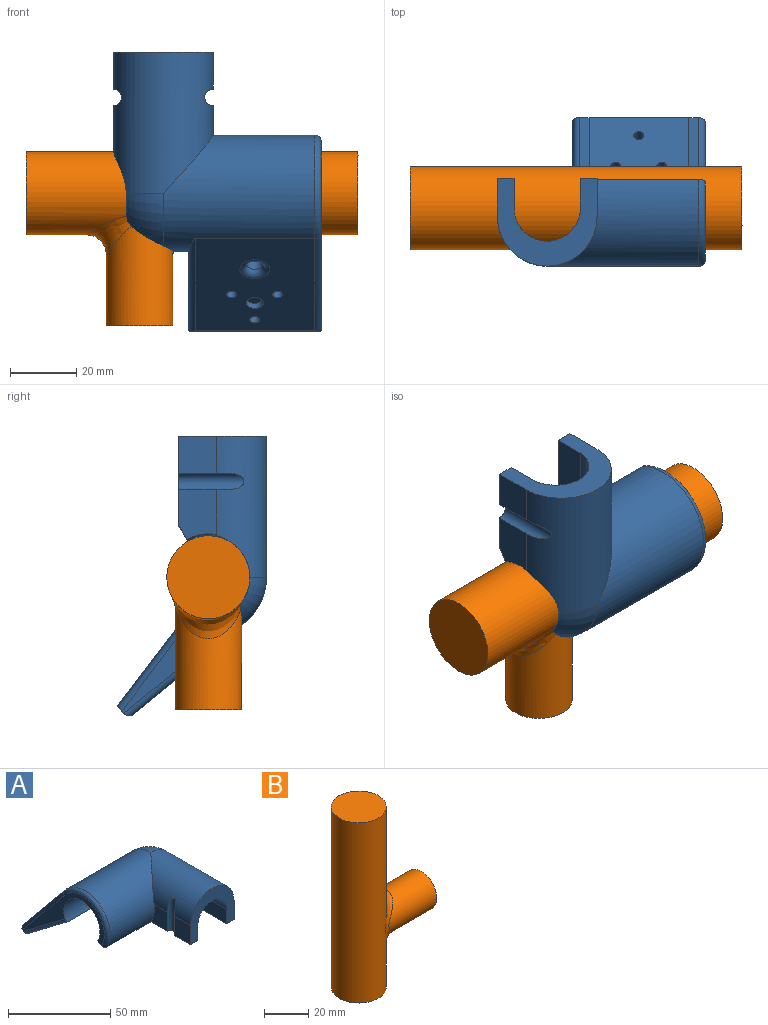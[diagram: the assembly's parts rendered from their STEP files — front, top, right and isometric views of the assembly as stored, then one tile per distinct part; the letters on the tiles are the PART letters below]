
ASSEMBLY  parts=2 mates=1
PART A: 48 faces, bbox 65.9x85.4x46.9 mm
  f0: cylinder r=15mm len=42.5mm, axis (0,1,0), area 1578.9mm2, adj f1,f2,f6,f7,f8,f9,f13,f16
  f1: plane 11.42x11.14mm, normal (-1,0,0), area 127.3mm2, adj f0,f9,f20,f34
  f2: cylinder r=17.5mm len=45.6mm, axis (1,0,0), area 2139mm2, adj f0,f5,f7,f15,f16,f26,f32,f42
  f3: cylinder r=17.5mm len=30mm, axis (1,0,0), area 226.4mm2, adj f4,f29,f30,f33
  f4: plane 30x4.35mm, normal (0,-0.49,-0.87), area 150mm2, adj f3,f13,f29,f33
  f5: plane 20.78x4.35mm, normal (0,-0.49,-0.87), area 81.6mm2, adj f2,f13,f16,f42
  f6: plane 11.43x11.14mm, normal (1,0,0), area 127.4mm2, adj f0,f9,f21,f25
  f7: plane 11.42x11.14mm, normal (-1,0,0), area 108.3mm2, adj f0,f2,f14,f20,f34
  f8: plane 15.33x11.78mm, normal (1,0,0), area 154.7mm2, adj f0,f10,f11,f21,f22,f24,f25
  f9: plane 30x26.43mm, normal (0,-1,0), area 360.7mm2, adj f0,f1,f6,f17,f18,f19,f20,f21
  f10: plane 4.47x0.28mm, normal (0,1,0), area 1.2mm2, adj f8,f11,f21,f22
  f11: plane 4.42x3.84mm, normal (0,0.49,-0.87), area 12.4mm2, adj f8,f10,f22
  f12: plane 56.55x41.54mm, normal (-1,0,0), area 353.8mm2, adj f13,f15,f27,f43,f44,f47
  f13: cylinder r=12.5mm len=62.04mm, axis (-1,0,0), area 2581.1mm2, adj f0,f4,f5,f12,f15,f16,f23,f24
  f14: plane 4.47x0.27mm, normal (0,1,0), area 1.2mm2, adj f7,f15,f20,f23
  f15: plane 37.02x4.35mm, normal (0,0.49,-0.87), area 174mm2, adj f2,f12,f13,f14,f23,f43
  f16: torus R=2.5mm, axis (-1,0,0), area 416mm2, adj f0,f2,f5,f13
  f17: cylinder r=10mm len=32.69mm, axis (0,-1,0), area 843.1mm2, adj f9,f18,f19,f22,f23,f24
  f18: plane 24.04x9.31mm, normal (1,0,0), area 210.7mm2, adj f9,f17,f20,f23
  f19: plane 24.04x8.58mm, normal (-1,0,0), area 194.7mm2, adj f9,f17,f21,f22
  f20: plane 27.29x5mm, normal (0,0,-1), area 126.2mm2, adj f1,f7,f9,f14,f18,f23,f34
  f21: plane 27.29x5mm, normal (0,0,-1), area 126.1mm2, adj f6,f8,f9,f10,f19,f22,f25
  f22: bspline ~10.16x9.21mm, area 75.8mm2, adj f8,f10,f11,f17,f19,f21,f24
  f23: bspline ~10.89x9.72mm, area 102.4mm2, adj f13,f14,f15,f17,f18,f20,f24
  f24: bspline ~36.01x14.54mm, area 311.2mm2, adj f0,f8,f13,f17,f22,f23
  f25: cylinder r=2.5mm len=19.65mm, axis (0,0,-1), area 138.8mm2, adj f0,f6,f8,f21
  f26: plane 36x33.53mm, normal (0,0.77,0.64), area 1458.5mm2, adj f2,f35,f37,f38,f39,f41,f44,f45
  f27: plane 40.2x2.51mm, normal (0,0.64,-0.77), area 118.2mm2, adj f12,f28,f30,f31,f32,f42,f45,f47
  f28: plane 27.87x21.17mm, normal (0,-0.6,-0.8), area 105mm2, adj f13,f27,f29,f47
  f29: plane 27.87x25.84mm, normal (1,0,0), area 114.4mm2, adj f3,f4,f28,f30
  f30: plane 30x25.84mm, normal (0,-0.77,-0.64), area 964mm2, adj f3,f27,f29,f33,f37,f38,f39,f40
  f31: plane 27.87x21.17mm, normal (0,-0.6,-0.8), area 105mm2, adj f13,f27,f33,f42
  f32: plane 29.63x25.22mm, normal (1,0,0), area 158.1mm2, adj f2,f27,f42,f46
  f33: plane 27.87x25.84mm, normal (-1,0,0), area 114.4mm2, adj f3,f4,f30,f31
  f34: cylinder r=2.5mm len=19.73mm, axis (0,0,-1), area 140.2mm2, adj f0,f1,f7,f20
  f35: cylinder r=2.6mm len=5.28mm, axis (0,0.77,0.64), area 32.7mm2, adj f26,f36
  f36: plane 5.2x4.01mm, normal (0,0.77,0.64), area 21.2mm2, adj f35
  f37: cylinder r=1.5mm len=5.77mm, axis (0,0.77,0.64), area 47.1mm2, adj f26,f30
  f38: cylinder r=1.5mm len=5.77mm, axis (0,0.77,0.64), area 47.1mm2, adj f26,f30
  f39: cylinder r=1.5mm len=5.77mm, axis (0,0.77,0.64), area 47.1mm2, adj f26,f30
  f40: cylinder r=2.5mm len=5.77mm, axis (0,-0.77,-0.64), area 47.1mm2, adj f30,f41
  f41: torus R=4.5mm, axis (0,-0.77,-0.64), area 63.7mm2, adj f26,f40
  f42: cylinder r=2mm len=29.46mm, axis (0,-0.8,0.6), area 100.8mm2, adj f2,f5,f27,f31,f32
  f43: torus R=15.5mm, axis (-1,0,0), area 157.4mm2, adj f2,f12,f15,f44
  f44: cylinder r=2mm len=36.36mm, axis (0,0.64,-0.77), area 139.7mm2, adj f12,f26,f43,f45
  f45: cylinder r=2mm len=40mm, axis (-1,0,0), area 119.4mm2, adj f26,f27,f44,f46
  f46: cylinder r=2mm len=36.35mm, axis (0,0.64,-0.77), area 127.4mm2, adj f2,f26,f32,f45
  f47: cylinder r=2mm len=29.81mm, axis (0,-0.8,0.6), area 111.4mm2, adj f12,f13,f27,f28
PART B: 6 faces, bbox 52.5x25x100 mm
  f0: cylinder r=12.5mm len=100mm, axis (0,0,-1), area 7234.1mm2, adj f1,f2,f5
  f1: plane 25x25mm, normal (0,0,1), area 490.9mm2, adj f0
  f2: plane 25x25mm, normal (0,0,-1), area 490.9mm2, adj f0
  f3: cylinder r=10mm len=30.72mm, axis (-1,0,0), area 1616.3mm2, adj f4,f5
  f4: plane 20x20mm, normal (1,0,0), area 314.2mm2, adj f3
  f5: bspline ~32.03x21.63mm, area 479.1mm2, adj f0,f3
PLACE A rot(axis=(0,-0.71,0.71),180deg) t=(13.67,13.12,25.61)mm
PLACE B rot(axis=(0,1,0),90deg) t=(-34.24,-4.38,30.61)mm
MATE cylindrical A.f13 <-> B.f0  axis (1,0,0) through (23.49,-4.38,30.61)mm
